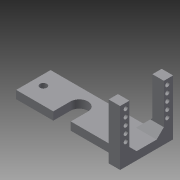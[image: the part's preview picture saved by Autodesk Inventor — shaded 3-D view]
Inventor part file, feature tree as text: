
AUTODESK INVENTOR PART (.ipt)
format: ipt  version: 2013 (Build 170138000, 138)  size: 174,592 bytes
history: native  units: mm
features: sketch x4, extrude x3, chamfer x3, hole x1
ambient origin geometry x8: Origin, YZ Plane, XZ Plane, XY Plane, X Axis, Y Axis, Z Axis, Center Point
bodies: Solid1 (feature_tree)
feature tree (11):
  extrude  "Extrusion1"  Depth=24.0mm
  extrude  "Extrusion2"  Depth=8.0mm
  chamfer  "Chamfer1"  Distance=38.6mm
  extrude  "Extrusion4"  Depth=6.5mm TaperAngle=45.0deg
  hole  "Hole2"  [1 undecoded]
  chamfer  "Chamfer2"  Distance=12.2mm
  chamfer  "Chamfer3"  Distance=50.0mm
  sketch  "Sketch1"  dims[d0=79.0mm d1=24.0mm]
  sketch  "Sketch3"  dims[d2=5.6mm d3=0.0mm d8=8.0mm]
  sketch  "Sketch5"  dims[d9=6.5mm]
  sketch  "Sketch6"  dims[d10=6.5mm d11=38.6mm d12=0.0mm d26=6.5mm d27=2.0mm d28=45.0deg d29=64.0mm d30=12.2mm d31=50.0mm d32=4.8mm d33=4.8mm d36=5.6mm d37=0.0mm d42=5.0mm d43=5.0mm d44=1.0mm d45=5.0mm d46=5.0mm d47=3.0mm d48=6.0mm d49=4.0mm d50=2.0mm d51=90.0deg d52=8.0mm d53=20.594885mm d54=33.0mm d55=1.0mm d56=6.4mm d57=2.0mm d58=45.0deg d59=5.0mm d60=5.0mm d61=5.0mm d62=5.0mm d63=5.0mm d64=2.0mm d65=45.0deg]
note: 1 required parameter value undecoded (feature->parameter linkage not recoverable at this tier; creation-order binding heuristic only, values carry confidence <= 0.55)
